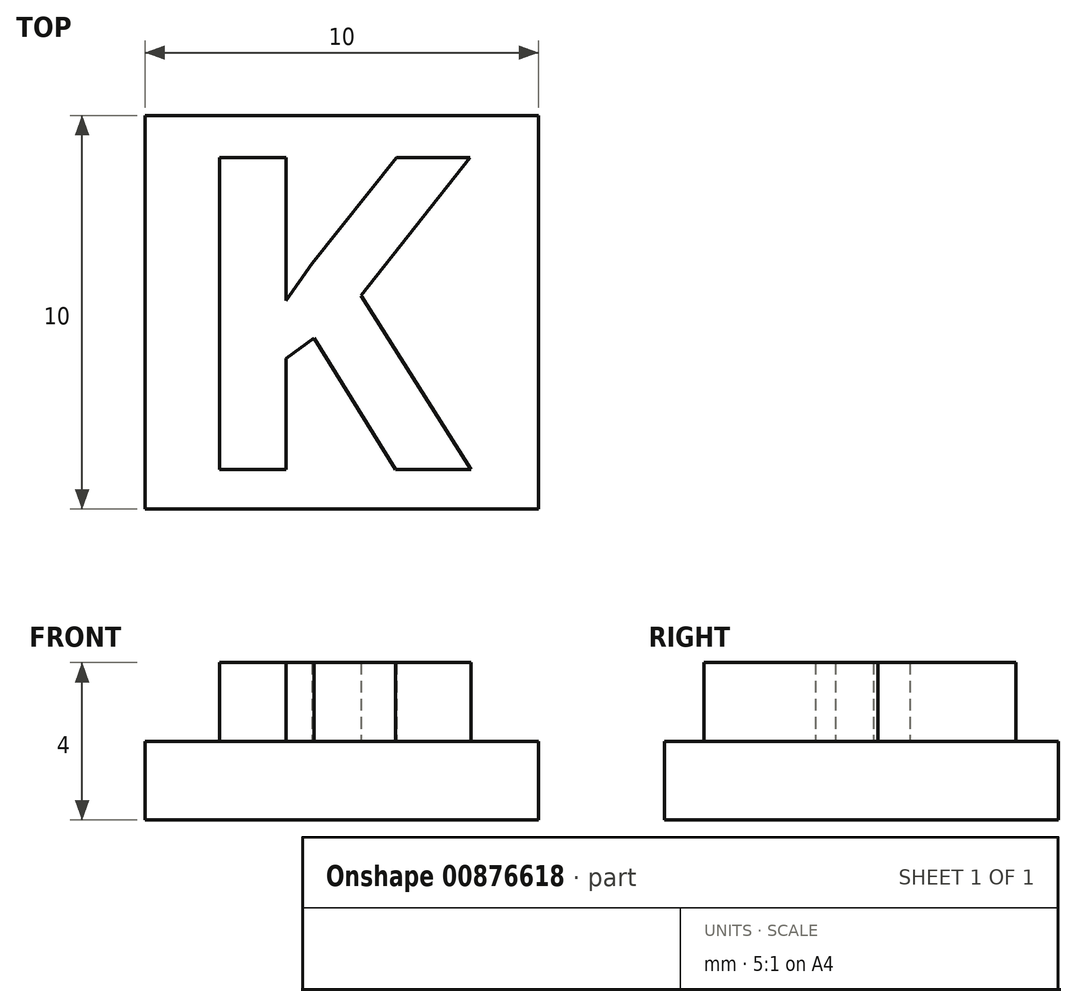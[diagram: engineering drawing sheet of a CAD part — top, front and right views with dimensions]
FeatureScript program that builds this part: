
annotation { "Feature Type Name" : "Feature", "Feature Type Description" : "" }
export const myFeature = defineFeature(function(context is Context, id is Id, definition is map)
    precondition{}
    {
        {
            var Q0;
            Q0=qCreatedBy(makeId("Top.planeOp"),FACE);
            var sketch = newSketch(context, id + "F0", { "sketchPlane" : qUnion([Q0])});
            skLineSegment(sketch, "E0.bottom", {"start": v(5, 5) * mm, "end": v(-5, 5) * mm});
            skLineSegment(sketch, "E0.top", {"start": v(5, -5) * mm, "end": v(-5, -5) * mm});
            skLineSegment(sketch, "E0.left", {"start": v(5, 5) * mm, "end": v(5, -5) * mm});
            skLineSegment(sketch, "E0.right", {"start": v(-5, 5) * mm, "end": v(-5, -5) * mm});
            skPoint(sketch, "E0.middle", {"position": v(0, 0) * mm});
            skSolve(sketch);
        }
        {
            var Q0;
            Q0=makeQuery(id+"F0.imprint","IMPRINT",FACE,{"disambiguationData":[TD([[makeQuery(id+"F0.imprint","IMPRINT",EDGE,{"derivedFrom":sQuery(id+"F0.wireOp",EDGE,"E0.bottom")}),1.0]])]});
            extrude(context, id + "F1", {"entities" : qUnion([Q0]), "depth" : 2 * mm, "offsetDistance" : 25 * mm});
        }
        {
            var Q0;
            Q0=makeQuery(id+"F1.opExtrude","CAP_FACE",FACE,{"disambiguationData":[OSD([sQuery(id+"F0.wireOp",EDGE,"E0.bottom"),sQuery(id+"F0.wireOp",EDGE,"E0.top"),sQuery(id+"F0.wireOp",EDGE,"E0.left"),sQuery(id+"F0.wireOp",EDGE,"E0.right")])],"isStart":false});
            var sketch = newSketch(context, id + "F2", { "sketchPlane" : qUnion([Q0])});
            skText(sketch, "E1", { "text": "K", "fontName": "OpenSans-Bold.ttf"});
            const initialGuessF2  = {"E1": [-0.0041, -0.004, 1, 0, 0.008]};
            skSetInitialGuess(sketch, initialGuessF2);
            skSolve(sketch);
        }
        {
            var Q0;
            Q0 = qSketchRegion(id + "F2", true);
            extrude(context, id + "F3", {"entities" : qUnion([Q0]), "operationType" : NewBodyOperationType.ADD, "depth" : 2 * mm, "offsetDistance" : 25 * mm});
        }
    });
